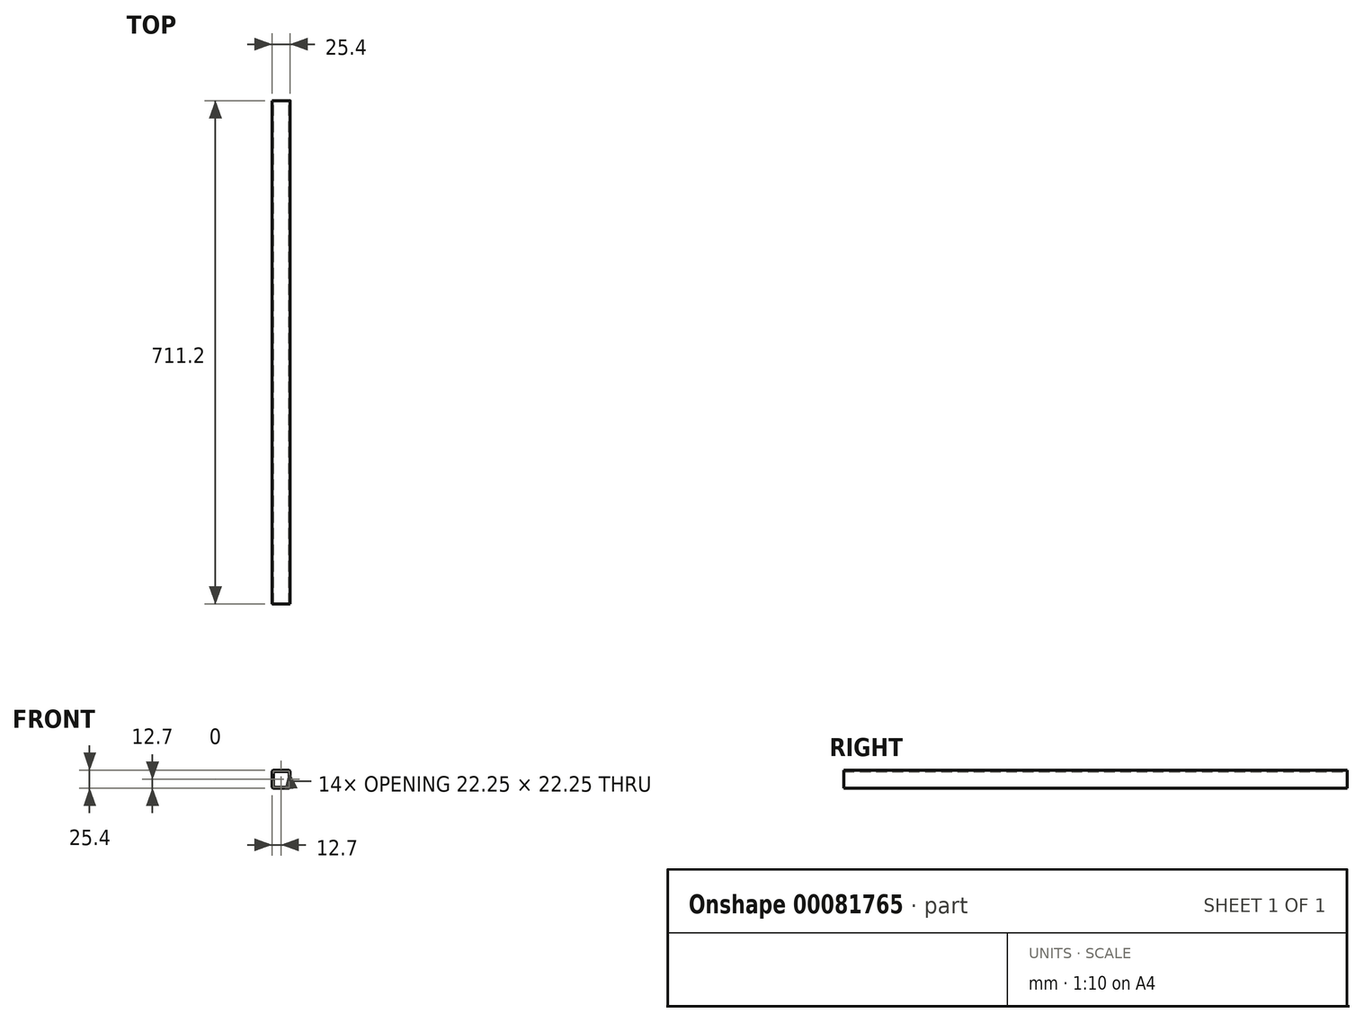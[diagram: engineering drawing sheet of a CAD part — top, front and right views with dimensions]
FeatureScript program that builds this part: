
annotation { "Feature Type Name" : "Feature", "Feature Type Description" : "" }
export const myFeature = defineFeature(function(context is Context, id is Id, definition is map)
    precondition{}
    {
        {
            var Q0;
            Q0=qCreatedBy(makeId("Front.planeOp"),FACE);
            var sketch = newSketch(context, id + "F0", { "sketchPlane" : qUnion([Q0])});
            skLineSegment(sketch, "E0.bottom", {"start": v(-10.62, -12.7) * mm, "end": v(10.62, -12.7) * mm});
            skLineSegment(sketch, "E0.top", {"start": v(-10.62, 12.7) * mm, "end": v(10.62, 12.7) * mm});
            skLineSegment(sketch, "E0.left", {"start": v(-12.7, -10.62) * mm, "end": v(-12.7, 10.62) * mm});
            skLineSegment(sketch, "E0.right", {"start": v(12.7, -10.62) * mm, "end": v(12.7, 10.62) * mm});
            skPoint(sketch, "E0.middle", {"position": v(0, 0) * mm});
            skLineSegment(sketch, "E1.bottom", {"start": v(10.62, -11.13) * mm, "end": v(-10.62, -11.13) * mm});
            skLineSegment(sketch, "E1.top", {"start": v(10.62, 11.13) * mm, "end": v(-10.62, 11.13) * mm});
            skLineSegment(sketch, "E1.left", {"start": v(11.13, -10.62) * mm, "end": v(11.13, 10.62) * mm});
            skLineSegment(sketch, "E1.right", {"start": v(-11.13, -10.62) * mm, "end": v(-11.13, 10.62) * mm});
            skPoint(sketch, "E2.visualSharp", {"position": v(-11.13, 11.13) * mm});
            skArc(sketch, "E2.filletArc", {"start": v(-10.62, 11.13) * mm, "mid": v(-10.98, 10.98) * mm, "end": v(-11.13, 10.62) * mm});
            skPoint(sketch, "E3.visualSharp", {"position": v(11.13, 11.13) * mm});
            skArc(sketch, "E3.filletArc", {"start": v(11.13, 10.62) * mm, "mid": v(10.98, 10.98) * mm, "end": v(10.62, 11.13) * mm});
            skPoint(sketch, "E4.visualSharp", {"position": v(11.13, -11.13) * mm});
            skArc(sketch, "E4.filletArc", {"start": v(10.62, -11.13) * mm, "mid": v(10.98, -10.98) * mm, "end": v(11.13, -10.62) * mm});
            skPoint(sketch, "E5.visualSharp", {"position": v(-11.13, -11.13) * mm});
            skArc(sketch, "E5.filletArc", {"start": v(-11.13, -10.62) * mm, "mid": v(-10.98, -10.98) * mm, "end": v(-10.62, -11.13) * mm});
            skPoint(sketch, "E6.visualSharp", {"position": v(-12.7, 12.7) * mm});
            skArc(sketch, "E6.filletArc", {"start": v(-10.62, 12.7) * mm, "mid": v(-12.09, 12.09) * mm, "end": v(-12.7, 10.62) * mm});
            skPoint(sketch, "E7.visualSharp", {"position": v(12.7, 12.7) * mm});
            skArc(sketch, "E7.filletArc", {"start": v(12.7, 10.62) * mm, "mid": v(12.09, 12.09) * mm, "end": v(10.62, 12.7) * mm});
            skPoint(sketch, "E8.visualSharp", {"position": v(-12.7, -12.7) * mm});
            skArc(sketch, "E8.filletArc", {"start": v(-12.7, -10.62) * mm, "mid": v(-12.09, -12.09) * mm, "end": v(-10.62, -12.7) * mm});
            skPoint(sketch, "E9.visualSharp", {"position": v(12.7, -12.7) * mm});
            skArc(sketch, "E9.filletArc", {"start": v(10.62, -12.7) * mm, "mid": v(12.09, -12.09) * mm, "end": v(12.7, -10.62) * mm});
            skSolve(sketch);
        }
        {
            var Q0;
            Q0=makeQuery(id+"F0.imprint","IMPRINT",FACE,{"disambiguationData":[TD([[makeQuery(id+"F0.imprint","IMPRINT",EDGE,{"derivedFrom":sQuery(id+"F0.wireOp",EDGE,"E0.bottom")}),1.0]])]});
            extrude(context, id + "F1", {"entities" : qUnion([Q0]), "depth" : 711.2 * mm, "offsetDistance" : 25.4 * mm});
        }
    });
